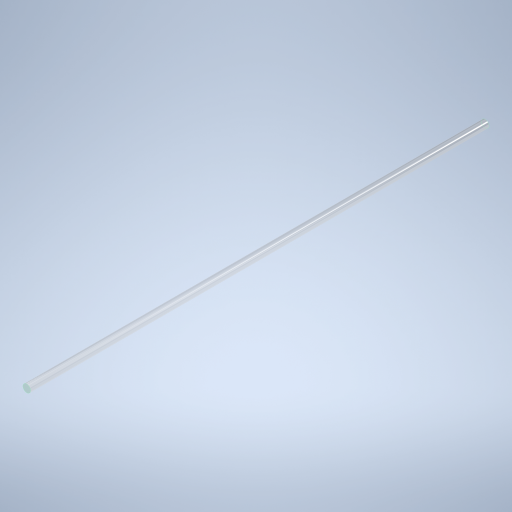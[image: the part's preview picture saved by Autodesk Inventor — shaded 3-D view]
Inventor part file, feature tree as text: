
AUTODESK INVENTOR PART (.ipt)
format: ipt  version: 2024 (Build 280153000, 153)  size: 228,864 bytes
history: native  units: in
note: dims shown in document units (in); Inventor stores cm internally (conversion verified against a paired STEP export)
features: extrude x1, sketch x1
ambient origin geometry x8: Origin, YZ Plane, XZ Plane, XY Plane, X Axis, Y Axis, Z Axis, Center Point
bodies: Solid1 (feature_tree)
feature tree (2):
  extrude  "Extrusion1"  Depth=11.811in TaperAngle=0.0deg
  sketch  "Sketch1"  dims[d0=0.1969in d1=11.811in d2=0.0in]
